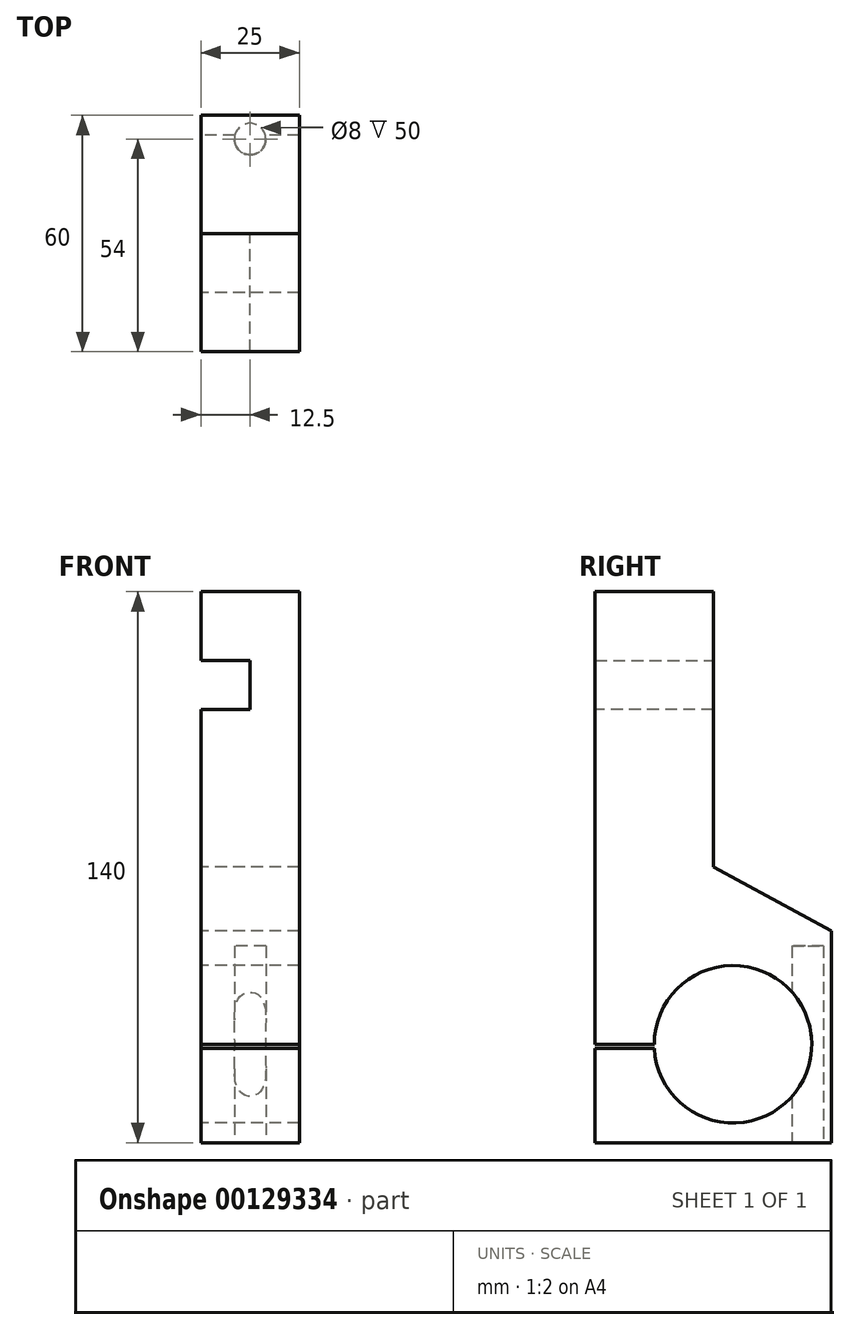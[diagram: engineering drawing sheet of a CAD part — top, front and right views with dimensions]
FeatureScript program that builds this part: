
annotation { "Feature Type Name" : "Feature", "Feature Type Description" : "" }
export const myFeature = defineFeature(function(context is Context, id is Id, definition is map)
    precondition{}
    {
        {
            var Q0;
            Q0=qCreatedBy(makeId("Right.planeOp"),FACE);
            var sketch = newSketch(context, id + "F0", { "sketchPlane" : qUnion([Q0])});
            skLineSegment(sketch, "E0.bottom", {"start": v(0, 0) * mm, "end": v(-60, 0) * mm});
            skLineSegment(sketch, "E0.top", {"start": v(-30, 140) * mm, "end": v(-60, 140) * mm});
            skLineSegment(sketch, "E0.left", {"start": v(0, 0) * mm, "end": v(0, 53.75) * mm});
            skLineSegment(sketch, "E0.right", {"start": v(-60, 0) * mm, "end": v(-60, 24) * mm});
            skLineSegment(sketch, "E1", {"start": v(-60, 25) * mm, "end": v(-45, 25) * mm});
            skArc(sketch, "E2", {"start": v(-44.97, 24) * mm, "mid": v(-5, 25.5) * mm, "end": v(-45, 25) * mm});
            skLineSegment(sketch, "E3", {"start": v(-30, 140) * mm, "end": v(-30, 70) * mm});
            skLineSegment(sketch, "E4", {"start": v(-30, 70) * mm, "end": v(0, 53.75) * mm});
            skPoint(sketch, "E5.orphan", {"position": v(0, 140) * mm});
            skLineSegment(sketch, "E6.0", {"start": v(-60, 24) * mm, "end": v(-44.97, 24) * mm});
            skLineSegment(sketch, "E7.trimOffspring", {"start": v(-60, 25) * mm, "end": v(-60, 140) * mm});
            skLineSegment(sketch, "E8", {"start": v(-60, 0) * mm, "end": v(-60, 12) * mm});
            skSolve(sketch);
        }
        {
            var Q0;
            Q0=makeQuery(id+"F0.imprint","IMPRINT",FACE,{"disambiguationData":[TD([[makeQuery(id+"F0.imprint","IMPRINT",EDGE,{"derivedFrom":sQuery(id+"F0.wireOp",EDGE,"E0.bottom")}),-1.0]])]});
            extrude(context, id + "F1", {"entities" : qUnion([Q0]), "depth" : 25 * mm});
        }
        {
            var Q0;
            Q0=qCreatedBy(makeId("Top.planeOp"),FACE);
            var sketch = newSketch(context, id + "F2", { "sketchPlane" : qUnion([Q0])});
            skLineSegment(sketch, "E9", {"start": v(0, 0) * mm, "end": v(12.5, 0) * mm});
            skLineSegment(sketch, "E10", {"start": v(12.5, 0) * mm, "end": v(12.5, -6) * mm});
            skCircle(sketch, "E11", {"center": v(12.5, -6) * mm, "radius": 4 * mm});
            skSolve(sketch);
        }
        {
            var Q0;
            Q0=makeQuery(id+"F2.imprint","IMPRINT",FACE,{"disambiguationData":[TD([[makeQuery(id+"F2.imprint","IMPRINT",EDGE,{"derivedFrom":sQuery(id+"F2.wireOp",EDGE,"E11")}),1.0]])]});
            extrude(context, id + "F3", {"entities" : qUnion([Q0]), "operationType" : NewBodyOperationType.REMOVE, "depth" : 50 * mm});
        }
        {
            var Q0;
            Q0=qCreatedBy(makeId("Front.planeOp"),FACE);
            var sketch = newSketch(context, id + "F4", { "sketchPlane" : qUnion([Q0])});
            skLineSegment(sketch, "E12", {"start": v(0, 0) * mm, "end": v(0, 110) * mm});
            skLineSegment(sketch, "E13", {"start": v(0, 110) * mm, "end": v(12.5, 110) * mm});
            skLineSegment(sketch, "E14", {"start": v(12.5, 110) * mm, "end": v(12.5, 122.5) * mm});
            skLineSegment(sketch, "E15", {"start": v(12.5, 122.5) * mm, "end": v(-7.74, 122.5) * mm});
            skLineSegment(sketch, "E16", {"start": v(-7.74, 122.5) * mm, "end": v(-7.74, 110) * mm});
            skLineSegment(sketch, "E17", {"start": v(-7.74, 110) * mm, "end": v(0, 110) * mm});
            skSolve(sketch);
        }
        {
            var Q0;
            Q0=makeQuery(id+"F4.imprint","IMPRINT",FACE,{"disambiguationData":[TD([[makeQuery(id+"F4.imprint","IMPRINT",EDGE,{"derivedFrom":sQuery(id+"F4.wireOp",EDGE,"E13")}),1.0]])]});
            extrude(context, id + "F5", {"entities" : qUnion([Q0]), "operationType" : NewBodyOperationType.REMOVE, "depth" : 60 * mm});
        }
    });
